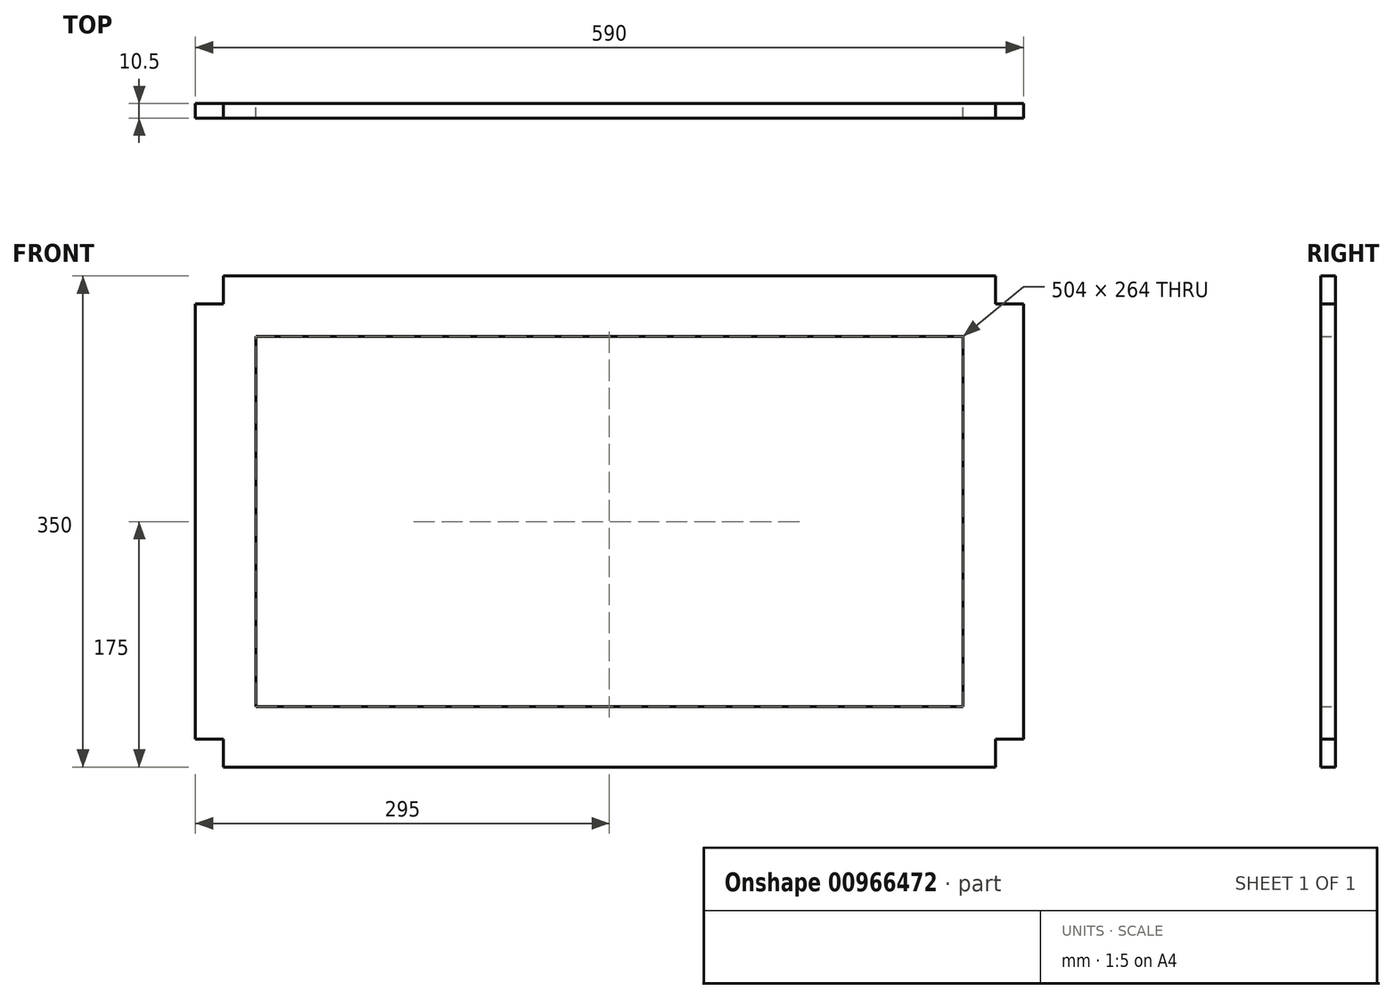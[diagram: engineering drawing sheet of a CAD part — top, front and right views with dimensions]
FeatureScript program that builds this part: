
annotation { "Feature Type Name" : "Feature", "Feature Type Description" : "" }
export const myFeature = defineFeature(function(context is Context, id is Id, definition is map)
    precondition{}
    {
        {
            var Q0;
            Q0=qCreatedBy(makeId("Front.planeOp"),FACE);
            var sketch = newSketch(context, id + "F0", { "sketchPlane" : qUnion([Q0])});
            skLineSegment(sketch, "E0.bottom", {"start": v(275, 175) * mm, "end": v(-275, 175) * mm});
            skLineSegment(sketch, "E0.top", {"start": v(275, -175) * mm, "end": v(-275, -175) * mm});
            skLineSegment(sketch, "E0.left", {"start": v(295, 155) * mm, "end": v(295, -155) * mm});
            skLineSegment(sketch, "E0.right", {"start": v(-295, 155) * mm, "end": v(-295, -155) * mm});
            skPoint(sketch, "E0.middle", {"position": v(0, 0) * mm});
            skLineSegment(sketch, "E1.top", {"start": v(-295, 155) * mm, "end": v(-275, 155) * mm});
            skLineSegment(sketch, "E1.right", {"start": v(-275, 175) * mm, "end": v(-275, 155) * mm});
            skLineSegment(sketch, "E2.top", {"start": v(295, 155) * mm, "end": v(275, 155) * mm});
            skLineSegment(sketch, "E2.right", {"start": v(275, 175) * mm, "end": v(275, 155) * mm});
            skLineSegment(sketch, "E3.top", {"start": v(-295, -155) * mm, "end": v(-275, -155) * mm});
            skLineSegment(sketch, "E3.right", {"start": v(-275, -175) * mm, "end": v(-275, -155) * mm});
            skLineSegment(sketch, "E4.top", {"start": v(295, -155) * mm, "end": v(275, -155) * mm});
            skLineSegment(sketch, "E4.right", {"start": v(275, -175) * mm, "end": v(275, -155) * mm});
            skPoint(sketch, "E5.orphan", {"position": v(-295, 175) * mm});
            skPoint(sketch, "E2.left.start.orphan", {"position": v(295, 175) * mm});
            skPoint(sketch, "E6.orphan", {"position": v(295, -175) * mm});
            skPoint(sketch, "E3.left.start.orphan", {"position": v(-295, -175) * mm});
            skLineSegment(sketch, "E7.0", {"start": v(295, 132) * mm, "end": v(-295, 132) * mm});
            skLineSegment(sketch, "E8.0", {"start": v(252, 132) * mm, "end": v(252, -132) * mm});
            skLineSegment(sketch, "E9.0", {"start": v(295, -132) * mm, "end": v(-295, -132) * mm});
            skLineSegment(sketch, "E10.0", {"start": v(-252, 132) * mm, "end": v(-252, -132) * mm});
            skSolve(sketch);
        }
        {
            var Q0;
            Q0 = qSketchRegion(id + "F0", true);
            extrude(context, id + "F1", {"entities" : qUnion([Q0]), "depth" : 10.5 * mm, "offsetDistance" : 25 * mm});
        }
    });
